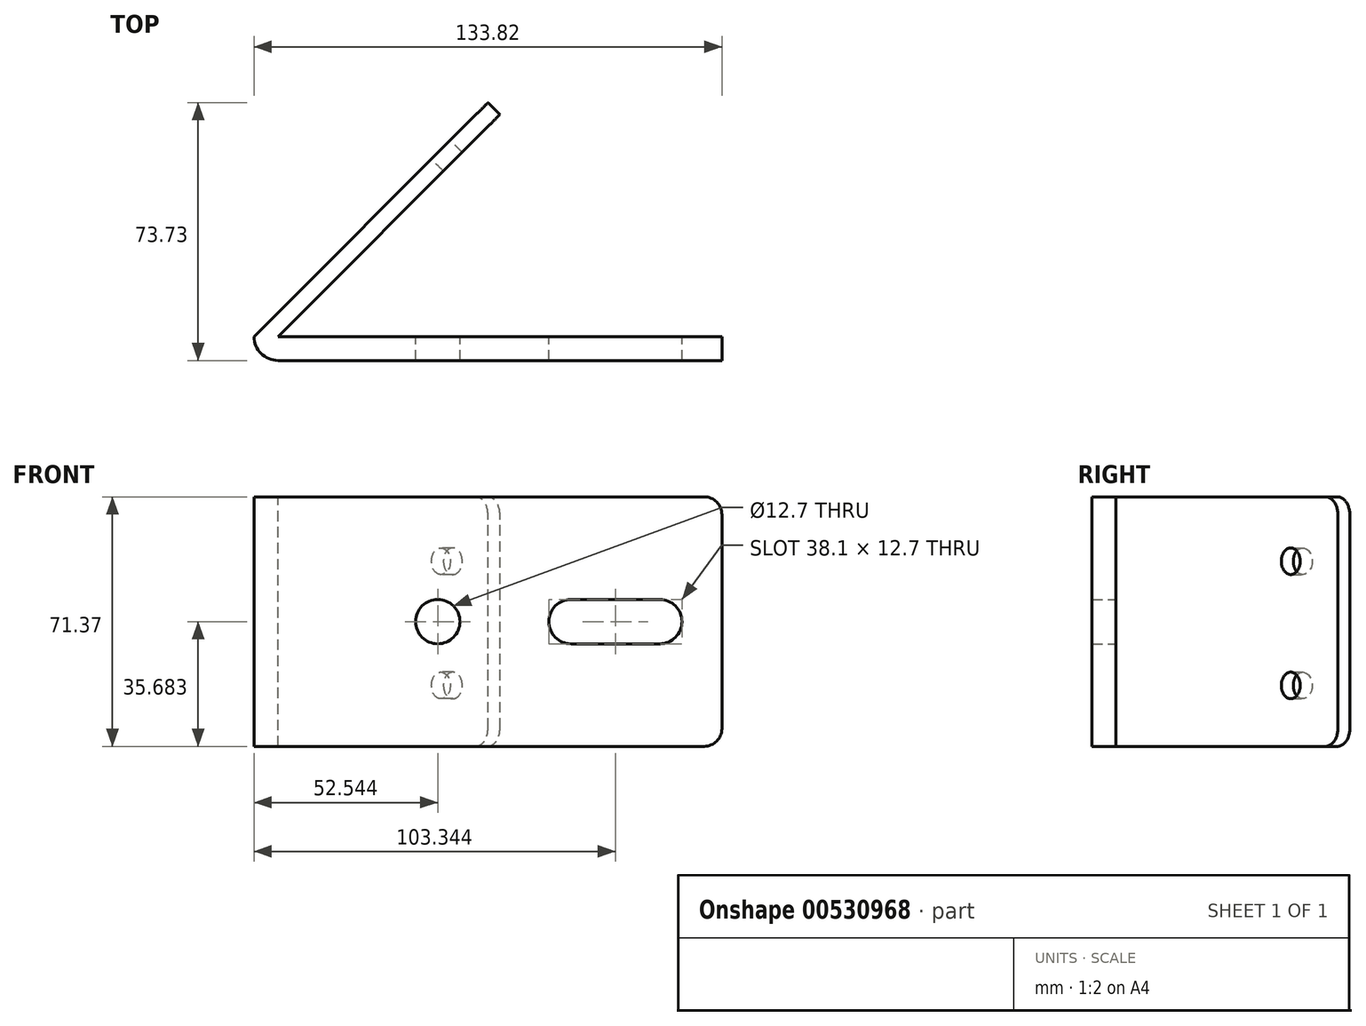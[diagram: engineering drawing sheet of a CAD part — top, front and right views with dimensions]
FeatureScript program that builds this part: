
annotation { "Feature Type Name" : "Feature", "Feature Type Description" : "" }
export const myFeature = defineFeature(function(context is Context, id is Id, definition is map)
    precondition{}
    {
        {
            var Q0;
            Q0=qCreatedBy(makeId("Top.planeOp"),FACE);
            var sketch = newSketch(context, id + "F0", { "sketchPlane" : qUnion([Q0])});
            skLineSegment(sketch, "E0", {"start": v(0, 0) * mm, "end": v(98.16, 0) * mm});
            skLineSegment(sketch, "E1", {"start": v(98.16, 0) * mm, "end": v(98.16, -6.82) * mm});
            skLineSegment(sketch, "E2", {"start": v(98.16, -6.82) * mm, "end": v(-28.84, -6.82) * mm});
            skArc(sketch, "E3", {"start": v(-28.84, -6.82) * mm, "mid": v(-33.66, -4.83) * mm, "end": v(-35.66, 0) * mm});
            skLineSegment(sketch, "E4", {"start": v(-35.66, 0) * mm, "end": v(31.25, 66.91) * mm});
            skLineSegment(sketch, "E5", {"start": v(31.25, 66.91) * mm, "end": v(34.66, 63.5) * mm});
            skLineSegment(sketch, "E6", {"start": v(-28.84, 0) * mm, "end": v(34.66, 63.5) * mm});
            skLineSegment(sketch, "E7", {"start": v(-28.84, 0) * mm, "end": v(0, 0) * mm});
            skSolve(sketch);
        }
        {
            var Q0;
            Q0=makeQuery(id+"F0.imprint","IMPRINT",FACE,{"disambiguationData":[TD([[makeQuery(id+"F0.imprint","IMPRINT",EDGE,{"derivedFrom":sQuery(id+"F0.wireOp",EDGE,"E0")}),-1.0]])]});
            extrude(context, id + "F1", {"entities" : qUnion([Q0]), "oppositeDirection" : true, "depth" : 71.37 * mm});
        }
        {
            var Q0;
            Q0=makeQuery(id+"F1.opExtrude","CAP_EDGE",EDGE,{"disambiguationData":[OSD([sQuery(id+"F0.wireOp",EDGE,"E5")])],"isStart":true});
            var Q1;
            Q1=makeQuery(id+"F1.opExtrude","CAP_EDGE",EDGE,{"disambiguationData":[OSD([sQuery(id+"F0.wireOp",EDGE,"E5")])],"isStart":false});
            var Q2;
            Q2=makeQuery(id+"F1.opExtrude","CAP_EDGE",EDGE,{"disambiguationData":[OSD([sQuery(id+"F0.wireOp",EDGE,"E1")])],"isStart":true});
            var Q3;
            Q3=makeQuery(id+"F1.opExtrude","CAP_EDGE",EDGE,{"disambiguationData":[OSD([sQuery(id+"F0.wireOp",EDGE,"E1")])],"isStart":false});
            fillet(context, id + "F2", {"entities" : qUnion([Q0, Q1, Q2, Q3]), "radius" : 5.08 * mm, "tangentPropagation" : true, "allowEdgeOverflow" : false});
        }
        {
            var Q0;
            Q0=makeQuery(id+"F1.opExtrude","SWEPT_FACE",FACE,{"disambiguationData":[OSD([sQuery(id+"F0.wireOp",EDGE,"E7")])]});
            var sketch = newSketch(context, id + "F3", { "sketchPlane" : qUnion([Q0])});
            skCircle(sketch, "E8", {"center": v(-16.88, -35.69) * mm, "radius": 6.35 * mm});
            skPoint(sketch, "E8.centerSnap0", {"position": v(28.84, -35.69) * mm});
            skArc(sketch, "E9", {"start": v(-54.98, -29.34) * mm, "mid": v(-48.63, -35.69) * mm, "end": v(-54.98, -42.04) * mm});
            skLineSegment(sketch, "E10", {"start": v(-54.98, -42.04) * mm, "end": v(-80.38, -42.04) * mm});
            skLineSegment(sketch, "E11", {"start": v(-54.98, -29.34) * mm, "end": v(-80.38, -29.34) * mm});
            skArc(sketch, "E12", {"start": v(-80.38, -42.04) * mm, "mid": v(-86.73, -35.69) * mm, "end": v(-80.38, -29.34) * mm});
            skSolve(sketch);
        }
        {
            var Q0;
            Q0=makeQuery(id+"F3.imprint","IMPRINT",FACE,{"disambiguationData":[TD([[makeQuery(id+"F3.imprint","IMPRINT",EDGE,{"derivedFrom":sQuery(id+"F3.wireOp",EDGE,"E8")}),1.0]])]});
            extrude(context, id + "F4", {"entities" : qUnion([Q0]), "operationType" : NewBodyOperationType.REMOVE, "oppositeDirection" : true, "depth" : 25.4 * mm});
        }
        {
            var Q0;
            Q0=qSketchRegion(id+"F3",true);
            extrude(context, id + "F5", {"entities" : qUnion([Q0]), "operationType" : NewBodyOperationType.REMOVE, "oppositeDirection" : true, "depth" : 25.4 * mm});
        }
        {
            var Q0;
            Q0=makeQuery(id+"F1.opExtrude","SWEPT_FACE",FACE,{"disambiguationData":[OSD([sQuery(id+"F0.wireOp",EDGE,"E4")])]});
            var sketch = newSketch(context, id + "F6", { "sketchPlane" : qUnion([Q0])});
            skCircle(sketch, "E13", {"center": v(-50.36, -53.95) * mm, "radius": 3.81 * mm});
            skCircle(sketch, "E14", {"center": v(-50.36, -18.43) * mm, "radius": 3.81 * mm});
            skSolve(sketch);
        }
        {
            var Q0;
            Q0=makeQuery(id+"F6.imprint","IMPRINT",FACE,{"disambiguationData":[TD([[makeQuery(id+"F6.imprint","IMPRINT",EDGE,{"derivedFrom":sQuery(id+"F6.wireOp",EDGE,"E13")}),1.0]])]});
            var Q1;
            Q1=makeQuery(id+"F6.imprint","IMPRINT",FACE,{"disambiguationData":[TD([[makeQuery(id+"F6.imprint","IMPRINT",EDGE,{"derivedFrom":sQuery(id+"F6.wireOp",EDGE,"E14")}),1.0]])]});
            extrude(context, id + "F7", {"entities" : qUnion([Q0, Q1]), "operationType" : NewBodyOperationType.REMOVE, "oppositeDirection" : true, "depth" : 25.4 * mm});
        }
    });
